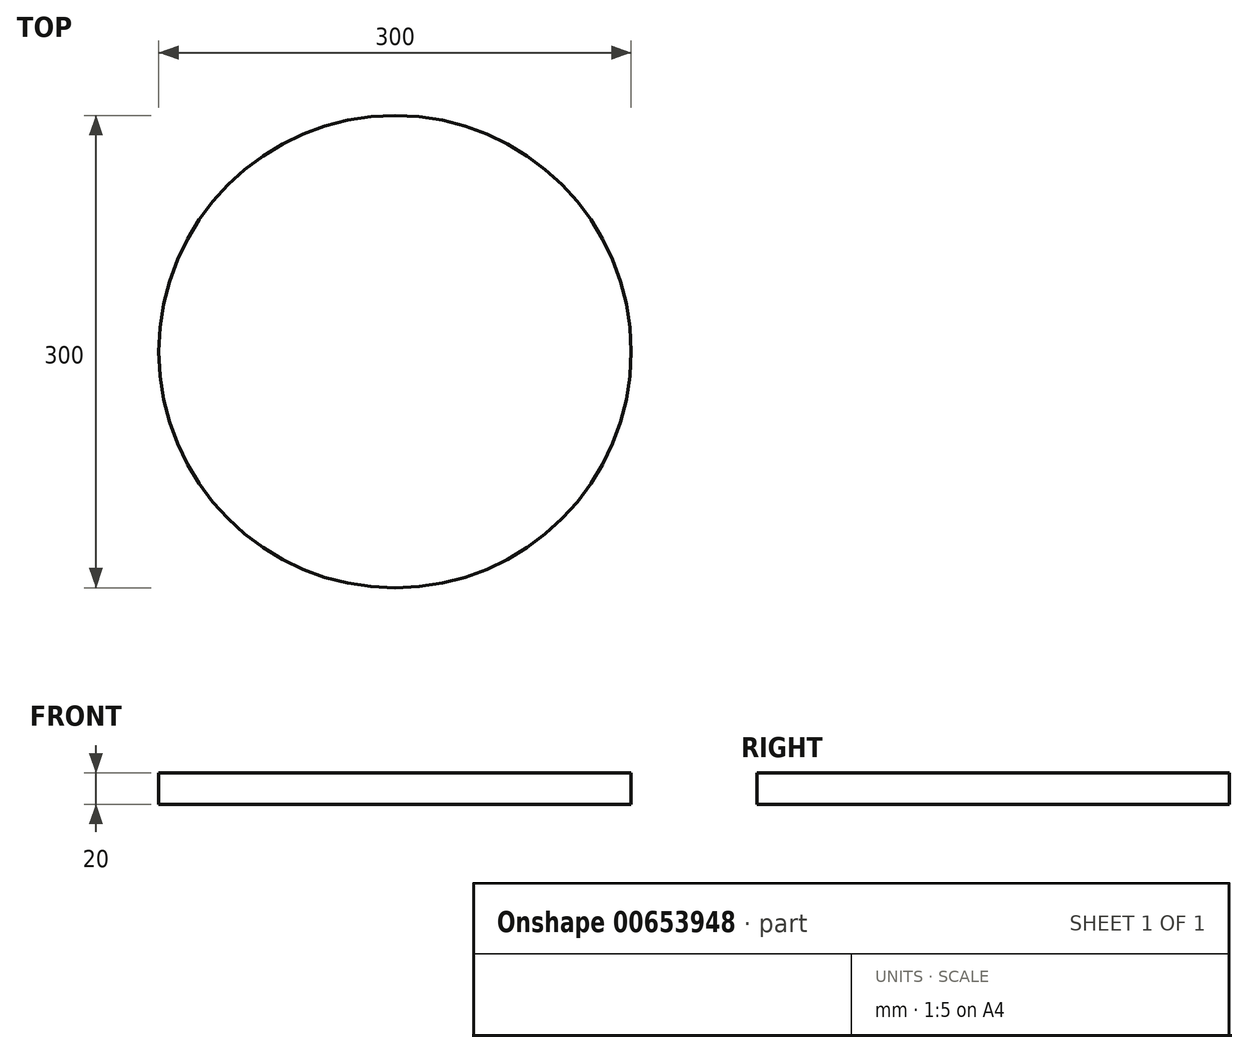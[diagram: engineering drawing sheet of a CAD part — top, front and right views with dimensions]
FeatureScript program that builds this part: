
annotation { "Feature Type Name" : "Feature", "Feature Type Description" : "" }
export const myFeature = defineFeature(function(context is Context, id is Id, definition is map)
    precondition{}
    {
        {
            var Q0;
            Q0=qCreatedBy(makeId("Top.planeOp"),FACE);
            var sketch = newSketch(context, id + "F0", { "sketchPlane" : qUnion([Q0])});
            skCircle(sketch, "E0", {"center": v(0, 0) * mm, "radius": 150 * mm});
            skSolve(sketch);
        }
        {
            var Q0;
            Q0=makeQuery(id+"F0.imprint","IMPRINT",FACE,{"disambiguationData":[TD([[makeQuery(id+"F0.imprint","IMPRINT",EDGE,{"derivedFrom":sQuery(id+"F0.wireOp",EDGE,"E0")}),1.0]])]});
            extrude(context, id + "F1", {"entities" : qUnion([Q0]), "depth" : 20 * mm, "offsetDistance" : 25 * mm});
        }
    });
